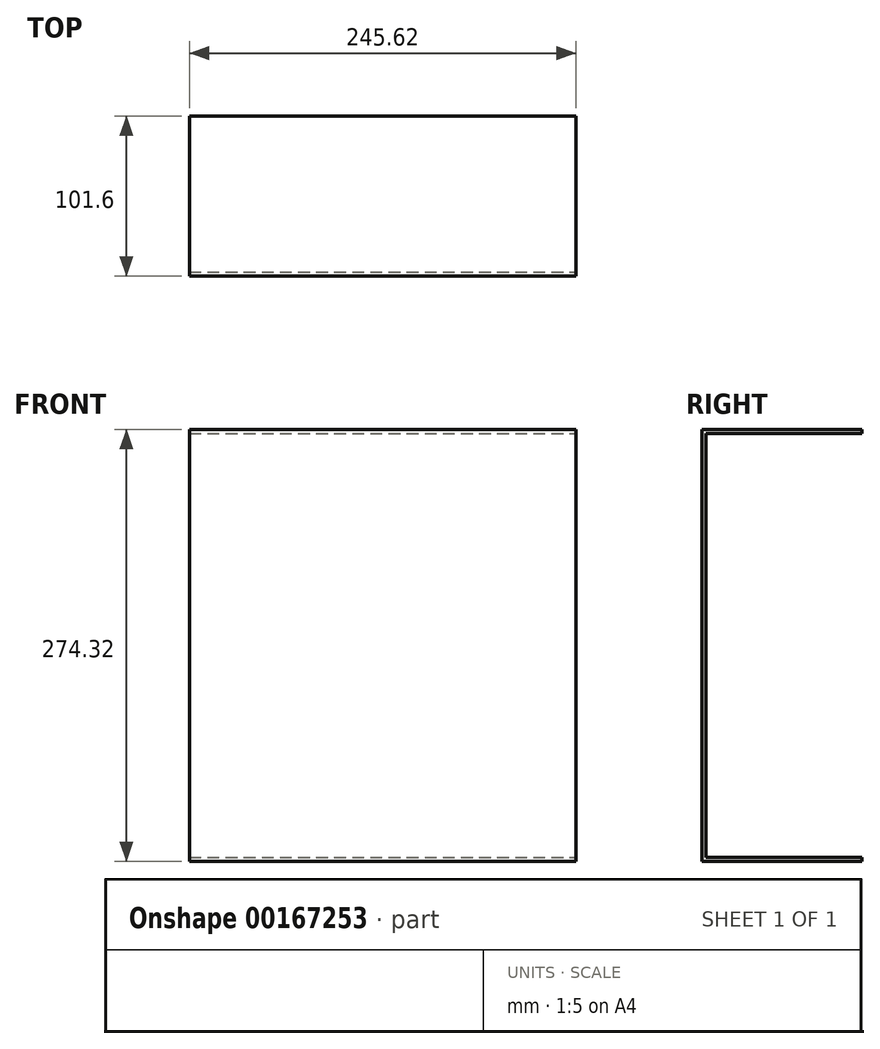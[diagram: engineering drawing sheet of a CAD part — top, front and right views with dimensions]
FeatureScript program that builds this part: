
annotation { "Feature Type Name" : "Feature", "Feature Type Description" : "" }
export const myFeature = defineFeature(function(context is Context, id is Id, definition is map)
    precondition{}
    {
        {
            var Q0;
            Q0=qCreatedBy(makeId("Front.planeOp"),FACE);
            var sketch = newSketch(context, id + "F0", { "sketchPlane" : qUnion([Q0])});
            skLineSegment(sketch, "E0.bottom", {"start": v(-179.35, 194.04) * mm, "end": v(66.27, 194.04) * mm});
            skLineSegment(sketch, "E0.top", {"start": v(-179.35, -80.28) * mm, "end": v(66.27, -80.28) * mm});
            skLineSegment(sketch, "E0.left", {"start": v(-179.35, 194.04) * mm, "end": v(-179.35, -80.28) * mm});
            skLineSegment(sketch, "E0.right", {"start": v(66.27, 194.04) * mm, "end": v(66.27, -80.28) * mm});
            skSolve(sketch);
        }
        {
            var Q0;
            Q0 = qSketchRegion(id + "F0", true);
            extrude(context, id + "F1", {"entities" : qUnion([Q0]), "depth" : 101.6 * mm});
        }
        {
            var Q0;
            Q0=makeQuery(id+"F1.opExtrude","CAP_FACE",FACE,{"disambiguationData":[OSD([sQuery(id+"F0.wireOp",EDGE,"E0.bottom"),sQuery(id+"F0.wireOp",EDGE,"E0.top"),sQuery(id+"F0.wireOp",EDGE,"E0.left"),sQuery(id+"F0.wireOp",EDGE,"E0.right")])],"isStart":true});
            var Q1;
            Q1=makeQuery(id+"F1.opExtrude","SWEPT_FACE",FACE,{"disambiguationData":[OSD([sQuery(id+"F0.wireOp",EDGE,"E0.left")])]});
            var Q2;
            Q2=makeQuery(id+"F1.opExtrude","SWEPT_FACE",FACE,{"disambiguationData":[OSD([sQuery(id+"F0.wireOp",EDGE,"E0.right")])]});
            shell(context, id + "F2", {"entities" : qUnion([Q0, Q1, Q2]), "thickness" : 2.54 * mm});
        }
    });
